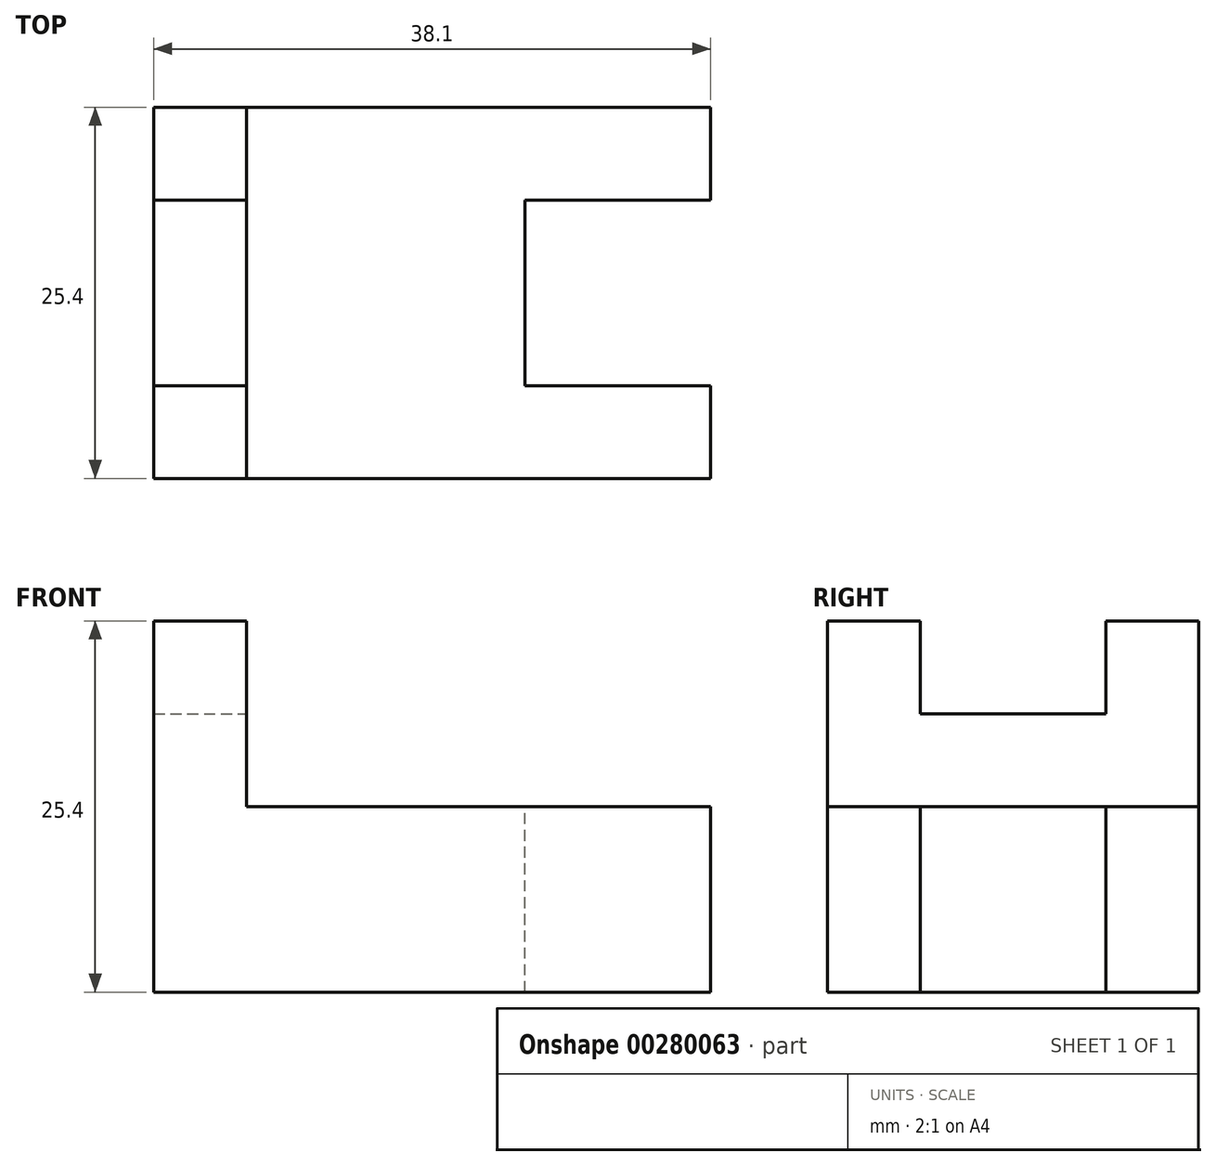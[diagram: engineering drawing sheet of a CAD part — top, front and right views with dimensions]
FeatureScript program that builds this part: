
annotation { "Feature Type Name" : "Feature", "Feature Type Description" : "" }
export const myFeature = defineFeature(function(context is Context, id is Id, definition is map)
    precondition{}
    {
        {
            var Q0;
            Q0=qCreatedBy(makeId("Front.planeOp"),FACE);
            var sketch = newSketch(context, id + "F0", { "sketchPlane" : qUnion([Q0])});
            skLineSegment(sketch, "E0.bottom", {"start": v(0, 0) * mm, "end": v(38.1, 0) * mm});
            skLineSegment(sketch, "E0.top", {"start": v(0, 25.4) * mm, "end": v(38.1, 25.4) * mm});
            skLineSegment(sketch, "E0.left", {"start": v(0, 0) * mm, "end": v(0, 25.4) * mm});
            skLineSegment(sketch, "E0.right", {"start": v(38.1, 0) * mm, "end": v(38.1, 25.4) * mm});
            skSolve(sketch);
        }
        {
            var Q0;
            Q0 = qSketchRegion(id + "F0", true);
            extrude(context, id + "F1", {"entities" : qUnion([Q0]), "depth" : 25.4 * mm});
        }
        {
            var Q0;
            Q0=makeQuery(id+"F1.opExtrude","SWEPT_FACE",FACE,{"disambiguationData":[OSD([sQuery(id+"F0.wireOp",EDGE,"E0.top")])]});
            var sketch = newSketch(context, id + "F2", { "sketchPlane" : qUnion([Q0])});
            skLineSegment(sketch, "E1.bottom", {"start": v(0, 0) * mm, "end": v(6.35, 0) * mm});
            skLineSegment(sketch, "E1.top", {"start": v(0, -25.4) * mm, "end": v(6.35, -25.4) * mm});
            skLineSegment(sketch, "E1.left", {"start": v(0, 0) * mm, "end": v(0, -25.4) * mm});
            skLineSegment(sketch, "E1.right", {"start": v(6.35, 0) * mm, "end": v(6.35, -25.4) * mm});
            skSolve(sketch);
        }
        {
            var Q0;
            {var subQ0=sQuery(id+"F2.wireOp",EDGE,"E1.right");Q0=makeQuery(id+"F2.imprint","IMPRINT",FACE,{"disambiguationData":[TD([[makeQuery(id+"F2.imprint","IMPRINT",EDGE,{"derivedFrom":subQ0}),1.0]])]});}
            extrude(context, id + "F3", {"entities" : qUnion([Q0]), "operationType" : NewBodyOperationType.REMOVE, "oppositeDirection" : true, "depth" : 12.7 * mm});
        }
        {
            var Q0;
            Q0=makeQuery(id+"F1.opExtrude","SWEPT_FACE",FACE,{"disambiguationData":[OSD([sQuery(id+"F0.wireOp",EDGE,"E0.top")])]});
            var sketch = newSketch(context, id + "F4", { "sketchPlane" : qUnion([Q0])});
            skLineSegment(sketch, "E2.bottom", {"start": v(0, 0) * mm, "end": v(6.35, 0) * mm});
            skLineSegment(sketch, "E2.top", {"start": v(0, -6.35) * mm, "end": v(6.35, -6.35) * mm});
            skLineSegment(sketch, "E2.left", {"start": v(0, 0) * mm, "end": v(0, -6.35) * mm});
            skLineSegment(sketch, "E2.right", {"start": v(6.35, 0) * mm, "end": v(6.35, -6.35) * mm});
            skLineSegment(sketch, "E3.bottom", {"start": v(0, -25.4) * mm, "end": v(6.35, -25.4) * mm});
            skLineSegment(sketch, "E3.top", {"start": v(0, -19.05) * mm, "end": v(6.35, -19.05) * mm});
            skLineSegment(sketch, "E3.left", {"start": v(0, -25.4) * mm, "end": v(0, -19.05) * mm});
            skLineSegment(sketch, "E3.right", {"start": v(6.35, -25.4) * mm, "end": v(6.35, -19.05) * mm});
            skSolve(sketch);
        }
        {
            var Q0;
            {var subQ0=sQuery(id+"F4.wireOp",EDGE,"E2.top");Q0=makeQuery(id+"F4.imprint","IMPRINT",FACE,{"disambiguationData":[TD([[makeQuery(id+"F4.imprint","IMPRINT",EDGE,{"derivedFrom":subQ0}),-1.0]])]});}
            extrude(context, id + "F5", {"entities" : qUnion([Q0]), "operationType" : NewBodyOperationType.REMOVE, "oppositeDirection" : true, "depth" : 6.35 * mm});
        }
        {
            var Q0;
            Q0=makeQuery(id+"F3.boolean.opBoolean","COPY",FACE,{"derivedFrom":makeQuery(id+"F3.opExtrude","CAP_FACE",FACE,{"disambiguationData":[OSD([sQuery(id+"F0.wireOp",EDGE,"E0.top"),sQuery(id+"F0.wireOp",EDGE,"E0.right"),sQuery(id+"F2.wireOp",EDGE,"E1.right")])],"isStart":false})});
            var sketch = newSketch(context, id + "F6", { "sketchPlane" : qUnion([Q0])});
            skPoint(sketch, "E4", {"position": v(38.1, 0) * mm});
            skPoint(sketch, "E5", {"position": v(38.1, -25.4) * mm});
            skPoint(sketch, "E6", {"position": v(38.1, -19.05) * mm});
            skPoint(sketch, "E7", {"position": v(25.4, -19.05) * mm});
            skPoint(sketch, "E8", {"position": v(38.1, -6.35) * mm});
            skPoint(sketch, "E9", {"position": v(25.4, -6.35) * mm});
            skLineSegment(sketch, "E10.bottom", {"start": v(25.4, -19.05) * mm, "end": v(38.1, -19.05) * mm});
            skLineSegment(sketch, "E10.top", {"start": v(25.4, -6.35) * mm, "end": v(38.1, -6.35) * mm});
            skLineSegment(sketch, "E10.left", {"start": v(25.4, -19.05) * mm, "end": v(25.4, -6.35) * mm});
            skLineSegment(sketch, "E10.right", {"start": v(38.1, -19.05) * mm, "end": v(38.1, -6.35) * mm});
            skSolve(sketch);
        }
        {
            var Q0;
            Q0=makeQuery(id+"F6.imprint","IMPRINT",FACE,{"disambiguationData":[TD([[makeQuery(id+"F6.imprint","IMPRINT",EDGE,{"derivedFrom":sQuery(id+"F6.wireOp",EDGE,"E10.bottom")}),1.0]])]});
            extrude(context, id + "F7", {"entities" : qUnion([Q0]), "operationType" : NewBodyOperationType.REMOVE, "endBound" : BoundingType.THROUGH_ALL, "oppositeDirection" : true, "depth" : 25.4 * mm});
        }
    });
